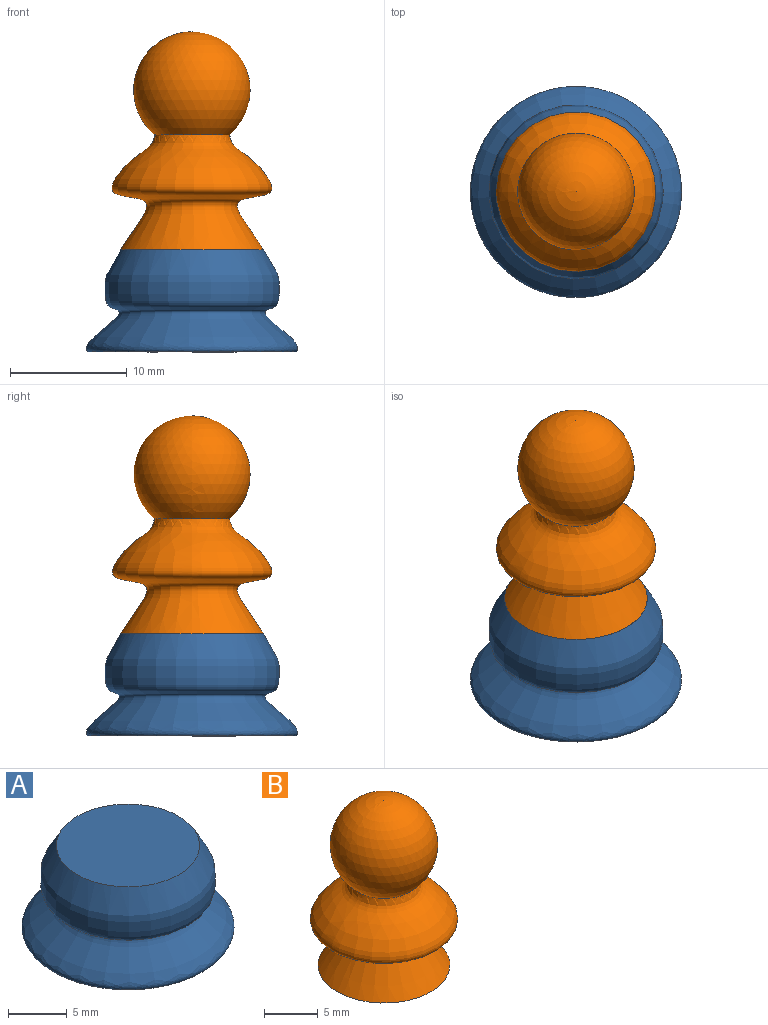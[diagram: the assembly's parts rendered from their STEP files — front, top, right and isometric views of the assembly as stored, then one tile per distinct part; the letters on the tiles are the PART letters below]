
ASSEMBLY  parts=2 mates=1
PART A: 3 faces, bbox 18.1x18.1x8.8 mm
  f0: plane 12.23x12.23mm, normal (0,0,1), area 117.5mm2, adj f1
  f1: revolved ~18.1x18.1mm, area 502.2mm2, adj f0,f2
  f2: cone r=8.96mm half-angle=89.7deg, axis (0,0,1), area 252.2mm2, adj f1
PART B: 3 faces, bbox 13.7x13.7x18.7 mm
  f0: revolved ~13.69x13.69mm, area 449.7mm2, adj f1,f2
  f1: plane 12.23x12.23mm, normal (0,0,-1), area 117.5mm2, adj f0
  f2: sphere r=5mm, area 277.7mm2, adj f0
PLACE A t=(-19.36,-5.8,-5.27)mm
PLACE B t=(-19.36,-5.8,8.07)mm
MATE fastened A.f2 <-> B.f1  axis (0,0,1) through (-19.36,-5.8,17.73)mm
